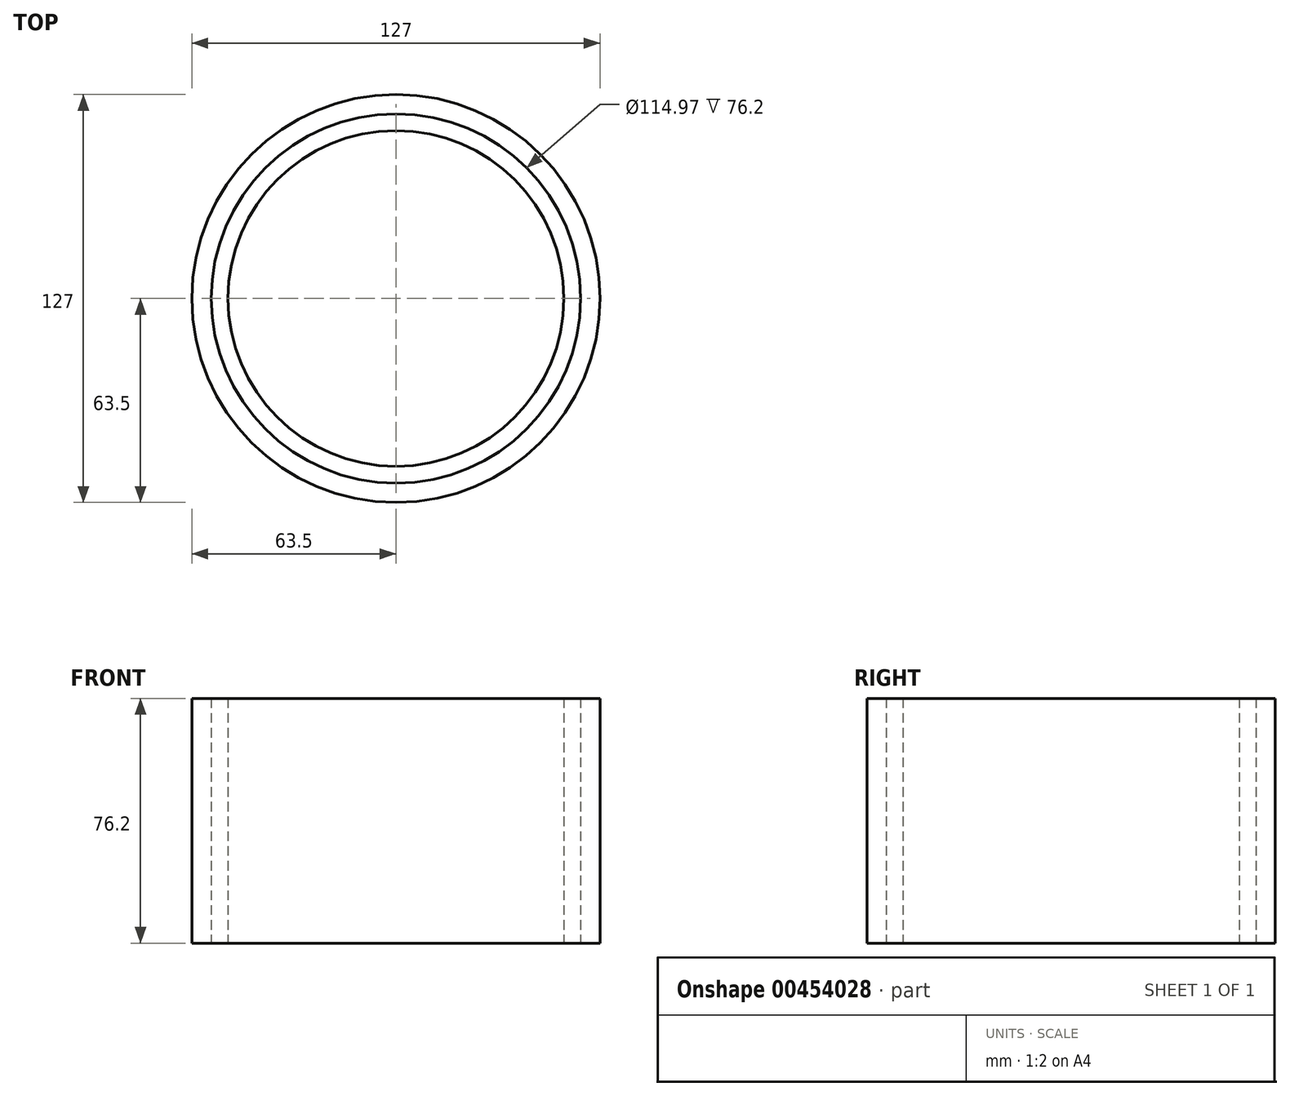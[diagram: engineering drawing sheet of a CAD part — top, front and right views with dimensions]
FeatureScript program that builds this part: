
annotation { "Feature Type Name" : "Feature", "Feature Type Description" : "" }
export const myFeature = defineFeature(function(context is Context, id is Id, definition is map)
    precondition{}
    {
        {
            var Q0;
            Q0=qCreatedBy(makeId("Top.planeOp"),FACE);
            var sketch = newSketch(context, id + "F0", { "sketchPlane" : qUnion([Q0])});
            skCircle(sketch, "E0", {"center": v(0, 0) * mm, "radius": 63.5 * mm});
            skSolve(sketch);
        }
        {
            var Q0;
            Q0 = qSketchRegion(id + "F0", true);
            extrude(context, id + "F1", {"entities" : qUnion([Q0]), "depth" : 76.2 * mm});
        }
        {
            var Q0;
            Q0=qCreatedBy(makeId("Top.planeOp"),FACE);
            var sketch = newSketch(context, id + "F2", { "sketchPlane" : qUnion([Q0])});
            skCircle(sketch, "E1", {"center": v(0, 0) * mm, "radius": 57.48 * mm});
            skCircle(sketch, "E2", {"center": v(0, 0) * mm, "radius": 52.27 * mm});
            skSolve(sketch);
        }
        {
            var Q0;
            Q0 = qSketchRegion(id + "F2", true);
            extrude(context, id + "F3", {"entities" : qUnion([Q0]), "operationType" : NewBodyOperationType.REMOVE, "depth" : 76.2 * mm});
        }
    });
